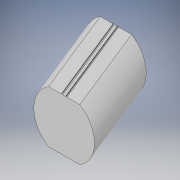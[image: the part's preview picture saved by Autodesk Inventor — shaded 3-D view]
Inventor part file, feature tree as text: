
AUTODESK INVENTOR PART (.ipt)
format: ipt  version: 2017 (Build 210142000, 142)  size: 135,168 bytes
history: native  units: in
note: dims shown in document units (in); Inventor stores cm internally (conversion verified against a paired STEP export)
features: sketch x2, other x1, plane x1
ambient origin geometry x8: Origin, YZ Plane, XZ Plane, XY Plane, X Axis, Y Axis, Z Axis, Center Point
bodies: Solid1 (feature_tree)
feature tree (4):
  other  "ramp"
  sketch  "Sketch1"  dims[d28=8.0in]
  plane  "Work Plane2"
  sketch  "Sketch6"  dims[d30=0.0in d31=0.0in d59=3.3333in d61=3.3333in d62=0.8521in d63=4.0in d64=0.5833in d65=3.8873in d66=3.8873in d67=1.7083in d68=0.0625in d69=0.0625in d70=1.6458in d71=0.25in d72=0.125in d73=0.0892in d74=0.0884in d75=45.0deg d76=3.3333in d77=0.125in]
